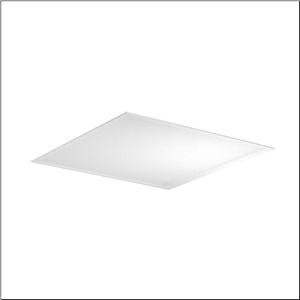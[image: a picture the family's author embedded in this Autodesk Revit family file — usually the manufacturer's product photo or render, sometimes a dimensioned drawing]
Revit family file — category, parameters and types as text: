
# Revit family: apollon_r__31_square_51mp12wd2m42_b676
name_source: partatom
category: Lighting Fixtures
units: mm (PartAtom-declared; Revit-internal decimal feet)

## family parameters
Cut with Voids When Loaded = No
Host = Face
Light Source = No
Part Type = Normal
Room Calculation Point = No
Round Connector Dimension = Use Diameter
Shared = No

## types (1)
- --- (1 x LED, 4000 lm, 27.5 W, 4000K)
    Apparent Load = 28 VA
    CIE Flux Codes = 62 87 97 100 100
    Color Rendering = 80
    Color Temperature = 4000K
    Default Elevation = 1800 mm
    Description = Apollon® 31 square, office luminaire, primary optical cover: micro prismatic cover, of PMMA, CAT 2 (L<= 3000cd/m²), light emission: direct distribution, primary light characteristic: symmetric, installation type: lay-in mounting, LED, rated luminous flux: 4.000lm, luminous efficacy: 142lm/W, light colour: 830/840, colour temperature: 3000/4000K, with terminal, 5-pole, mains connection: 220..240V, AC/DC, 0/50..60Hz, rated input power: 28W, housing, of aluminium, traffic white (RAL 9016), module: M600, length: 595mm, width: 595mm, height: 32mm, housing upper side, of sheet steel, galvanised, protection rating (complete): IP20, protection rating (on room side): IP40, insulation class (complete): insulation class II (safety insulation), certification: CE, ENEC, impact resistance: IK03, permissible operating ambient temperature: -20..+40°C, permissible storage temperature: -20..+60°C, packaging unit: 1 piece
    Height = 0 mm  [stored 0 ft]
    Lamp = 1 x LED
    Lamp Light Flux = 4000 lm
    Lamp Power = 27.5 W
    Lamp count = 1
    Length = 595 mm
    Luminous efficacy = 145 lm/W
    Manufacturer = Siteco
    ModVariant = No
    Model = 51MP12WD2M42
    Mounting Place = Ceiling
    Mounting Type = Recessed
    Number of Poles = 1
    OnlyDefault = Yes
    Power Factor = 1
    Product Name = Apollon® 31 square
    Product group = office luminaire | ceiling recessed
    ProductGroupID = 401
    Protection Class = Protection class II
    Protection Degree = IP 20
    RLX_Detail_Level = 1
    RLX_Emergency_Light_Flux = 0 lm
    RLX_Emergency_Type = 0
    RLX_Emergency_Type_DB = No
    RlxData = <blob elided: 12737 chars, md5=36bc5b9b>
    Socket = socket
    Standby Power = 0 W
    System Light Flux = 4000 lm
    System Power = 28 W
    Type Comments = factory setting: colour temperature 4000K
    Type Image = l_1291035.jpg
    URL = http://relux.com
    VarID = @adj_008993
    Voltage = 0 V
    Weight = 0.00 kg
    Width = 595 mm

note: [stored X ft] marks values corroborated as IEEE doubles in the binary element streams (Revit-internal decimal feet)

## geometry (parser evidence)
native form markers: Sweep x10
no freeform markers — native parametric forms only
